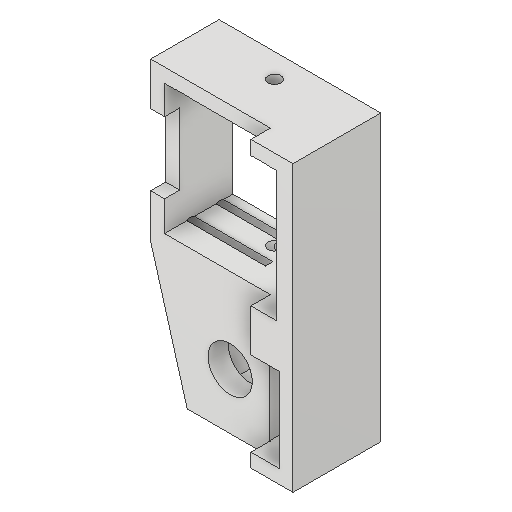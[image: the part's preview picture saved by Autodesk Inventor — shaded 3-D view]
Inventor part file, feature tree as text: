
AUTODESK INVENTOR PART (.ipt)
format: ipt  version: 2022 (Build 260153000, 153)  size: 243,200 bytes
history: native  units: mm
features: reference x14, sketch x5, extrude x5, other x3, plane x2, projected_geometry x2
ambient origin geometry x8: Origin, YZ Plane, XZ Plane, XY Plane, X Axis, Y Axis, Z Axis, Center Point
bodies: Solid1 (feature_tree)
feature tree (31):
  sketch  "Sketch1"  dims[d0=0.1mm d1=0.2mm]
  plane  "Work Plane1"
  extrude  "Extrusion1"  Depth=0.2mm
  sketch  "Sketch2"  dims[d2=3.0mm d3=3.0mm]
  plane  "Work Plane2"
  extrude  "Extrusion2"  Depth=3.0mm
  extrude  "Extrusion3"  Depth=3.0mm
  extrude  "Extrusion4"  Depth=3.0mm
  extrude  "Extrusion5"  Depth=18.2mm
  reference  "Reference1"
  reference  "Reference2"
  reference  "Reference3"
  reference  "Reference4"
  reference  "Reference5"
  reference  "Reference6"
  reference  "Reference7"
  reference  "Reference8"
  reference  "Reference9"
  projected_geometry  "Projected Loop1"
  reference  "Reference10"
  sketch  "Sketch3"  dims[d4=3.0mm d5=3.0mm]
  reference  "Reference11"
  reference  "Reference12"
  sketch  "Sketch4"  dims[d6=3.0mm d7=3.0mm]
  reference  "Reference13"
  sketch  "Sketch5"  dims[d8=10.0mm d9=0.0mm d10=18.2mm d11=10.0mm d12=0.0mm d13=2.8mm d14=2.8mm d15=20.0mm d16=0.0mm d17=20.0mm d18=0.0mm d19=20.0mm d20=0.0mm]
  projected_geometry  "Projected Loop2"
  reference  "Reference14"
  other  "Assembly_Nema_Motor_attachement_for_XYstage.iam"
  other  "00_NEMA11:1"
  other  "00_micrometer_moun_xystage_china:1"
